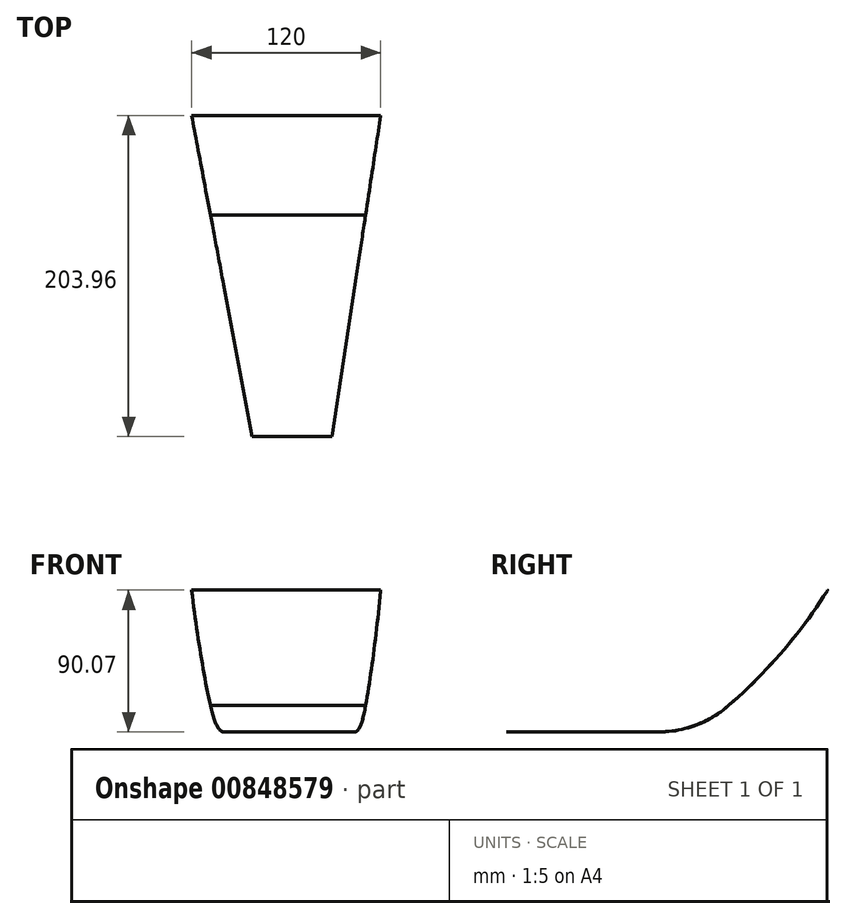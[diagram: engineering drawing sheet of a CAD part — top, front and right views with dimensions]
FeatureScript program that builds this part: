
annotation { "Feature Type Name" : "Feature", "Feature Type Description" : "" }
export const myFeature = defineFeature(function(context is Context, id is Id, definition is map)
    precondition{}
    {
        {
            var Q0;
            Q0=qCreatedBy(makeId("Right.planeOp"),FACE);
            var sketch = newSketch(context, id + "F0", { "sketchPlane" : qUnion([Q0])});
            skLineSegment(sketch, "E0", {"start": v(-73.7, 0) * mm, "end": v(23.08, 0) * mm});
            skArc(sketch, "E1", {"start": v(23.08, 0) * mm, "mid": v(46.67, 4.32) * mm, "end": v(67.2, 16.73) * mm});
            skArc(sketch, "E2", {"start": v(67.2, 16.73) * mm, "mid": v(101.42, 51) * mm, "end": v(130.18, 89.97) * mm});
            skArc(sketch, "E3.0", {"start": v(67.27, 16.65) * mm, "mid": v(101.5, 50.93) * mm, "end": v(130.26, 89.91) * mm});
            skArc(sketch, "E3.1", {"start": v(23.08, -0.1) * mm, "mid": v(46.7, 4.23) * mm, "end": v(67.27, 16.65) * mm});
            skLineSegment(sketch, "E3.2", {"start": v(-73.7, -0.1) * mm, "end": v(23.08, -0.1) * mm});
            skLineSegment(sketch, "E4", {"start": v(130.26, 89.91) * mm, "end": v(130.18, 89.97) * mm});
            skLineSegment(sketch, "E5", {"start": v(-73.7, -0.1) * mm, "end": v(-73.7, 0) * mm});
            skSolve(sketch);
        }
        {
            var Q0;
            Q0=qCreatedBy(makeId("Right.planeOp"),FACE);
            cPlane(context, id + "F1", {"entities" : qUnion([Q0]), "cplaneType" : CPlaneType.OFFSET, "offset" : 80 * mm, "width" : 150 * mm, "height" : 150 * mm});
        }
        {
            var Q0;
            Q0 = qSketchRegion(id + "F0", true);
            extrude(context, id + "F2", {"entities" : qUnion([Q0]), "depth" : 120 * mm, "offsetDistance" : 25 * mm});
        }
        {
            var Q0;
            Q0=qCreatedBy(makeId("Top.planeOp"),FACE);
            var sketch = newSketch(context, id + "F3", { "sketchPlane" : qUnion([Q0])});
            skLineSegment(sketch, "E6", {"start": v(0, -73.85) * mm, "end": v(38.47, -73.85) * mm});
            skLineSegment(sketch, "E7", {"start": v(38.47, -73.85) * mm, "end": v(0, 130.24) * mm});
            skLineSegment(sketch, "E8", {"start": v(0, 130.24) * mm, "end": v(-3.18, 133.67) * mm});
            skLineSegment(sketch, "E9", {"start": v(-3.18, 133.67) * mm, "end": v(-37.88, -99.64) * mm});
            skLineSegment(sketch, "E10", {"start": v(-37.88, -99.64) * mm, "end": v(0, -73.85) * mm});
            skLineSegment(sketch, "E11", {"start": v(120.1, -73.85) * mm, "end": v(89, -73.85) * mm});
            skPoint(sketch, "E11.startSnap0", {"position": v(19.24, -73.85) * mm});
            skLineSegment(sketch, "E12", {"start": v(89, -73.85) * mm, "end": v(120.04, 130.2) * mm});
            skLineSegment(sketch, "E13", {"start": v(120.04, 130.2) * mm, "end": v(121.7, 131.59) * mm});
            skLineSegment(sketch, "E14", {"start": v(121.7, 131.59) * mm, "end": v(134.19, 128.5) * mm});
            skLineSegment(sketch, "E15", {"start": v(134.19, 128.5) * mm, "end": v(258.56, -143.56) * mm});
            skLineSegment(sketch, "E16", {"start": v(258.56, -143.56) * mm, "end": v(120.1, -73.85) * mm});
            skSolve(sketch);
        }
        {
            var Q0;
            Q0 = qSketchRegion(id + "F3", true);
            extrude(context, id + "F4", {"entities" : qUnion([Q0]), "operationType" : NewBodyOperationType.REMOVE, "endBound" : BoundingType.SYMMETRIC, "depth" : 290 * mm, "offsetDistance" : 25 * mm});
        }
    });
